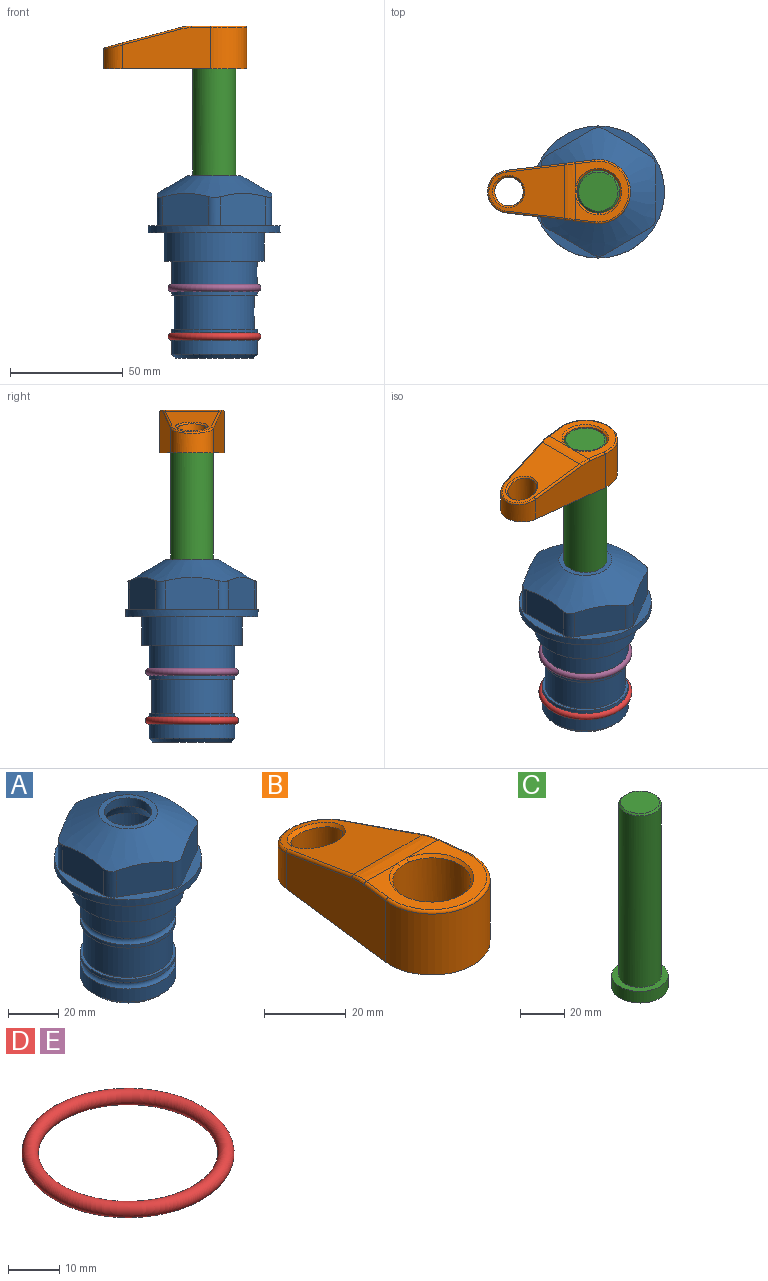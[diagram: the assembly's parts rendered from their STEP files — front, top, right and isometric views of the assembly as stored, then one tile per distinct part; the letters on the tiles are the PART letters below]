
ASSEMBLY  parts=5 mates=4
PART A: 36 faces, bbox 58.7x58.7x81 mm
  f0: cylinder r=17.78mm len=35.56mm, axis (0,0,1), area 1670.8mm2, adj f23,f24,f31
  f1: cylinder r=19.05mm len=38.1mm, axis (0,0,1), area 1191.9mm2, adj f26,f27,f30
  f2: plane 58.66x58.66mm, normal (0,0,-1), area 1150.6mm2, adj f3,f28
  f3: cylinder r=29.33mm len=58.66mm, axis (0,0,-1), area 585.1mm2, adj f2,f4
  f4: plane 58.66x58.66mm, normal (0,0,1), area 475.9mm2, adj f3,f5,f6,f7,f8,f9,f10,f11
  f5: plane 20.32x14.34mm, normal (-0.5,0.87,0), area 324.4mm2, adj f4,f15,f16,f17
  f6: plane 20.32x14.34mm, normal (0.5,0.87,0), area 324.4mm2, adj f4,f14,f15,f17
  f7: plane 23.48x14.34mm, normal (1,0,0), area 324.4mm2, adj f4,f13,f14,f17
  f8: plane 20.32x14.34mm, normal (0.5,-0.87,0), area 324.4mm2, adj f4,f12,f13,f17
  f9: plane 20.32x14.34mm, normal (-0.5,-0.87,0), area 324.4mm2, adj f4,f11,f12,f17
  f10: plane 23.48x14.34mm, normal (-1,0,0), area 324.4mm2, adj f4,f11,f16,f17
  f11: cylinder r=5.08mm len=12.85mm, axis (0,0,-1), area 67.2mm2, adj f4,f9,f10,f17
  f12: cylinder r=5.08mm len=12.85mm, axis (0,0,-1), area 67.2mm2, adj f4,f8,f9,f17
  f13: cylinder r=5.08mm len=12.85mm, axis (0,0,-1), area 67.2mm2, adj f4,f7,f8,f17
  f14: cylinder r=5.08mm len=12.85mm, axis (0,0,-1), area 67.2mm2, adj f4,f6,f7,f17
  f15: cylinder r=5.08mm len=12.85mm, axis (0,0,-1), area 67.2mm2, adj f4,f5,f6,f17
  f16: cylinder r=5.08mm len=12.85mm, axis (0,0,-1), area 67.2mm2, adj f4,f5,f10,f17
  f17: cone r=11.73mm half-angle=60deg, axis (0,0,-1), area 2071.8mm2, adj f5,f6,f7,f8,f9,f10,f11,f12
  f18: plane 23.46x23.46mm, normal (0,0,1), area 147.4mm2, adj f17,f35
  f19: plane 34.93x34.93mm, normal (0,0,-1), area 958mm2, adj f29
  f20: cylinder r=19.05mm len=38.1mm, axis (0,0,1), area 760.1mm2, adj f21,f29
  f21: torus R=19.05mm, axis (0,0,1), area 565.3mm2, adj f20,f22
  f22: cylinder r=19.05mm len=38.1mm, axis (0,0,1), area 190mm2, adj f21,f23
  f23: plane 38.1x38.1mm, normal (0,0,1), area 146.9mm2, adj f0,f22
  f24: plane 38.1x38.1mm, normal (0,0,-1), area 146.9mm2, adj f0,f25
  f25: cylinder r=19.05mm len=38.1mm, axis (0,0,1), area 190mm2, adj f24,f26
  f26: torus R=19.05mm, axis (0,0,1), area 565.3mm2, adj f1,f25
  f27: plane 44.45x44.45mm, normal (0,0,-1), area 411.7mm2, adj f1,f28
  f28: cylinder r=22.23mm len=44.45mm, axis (0,0,1), area 1773.5mm2, adj f2,f27
  f29: cone r=19.05mm half-angle=45deg, axis (0,0,1), area 257.5mm2, adj f19,f20
  f30: cylinder r=3.17mm len=6.75mm, axis (-1,0,0), area 128mm2, adj f1,f33
  f31: cylinder r=3.17mm len=6.35mm, axis (-1,0,0), area 102.5mm2, adj f0,f33
  f32: plane 25.4x25.4mm, normal (0,0,1), area 506.7mm2, adj f33
  f33: cylinder r=12.7mm len=66.42mm, axis (0,0,-1), area 5236.2mm2, adj f30,f31,f32,f34
  f34: cone r=9.53mm half-angle=30deg, axis (0,0,-1), area 443.4mm2, adj f33,f35
  f35: cylinder r=9.53mm len=19.05mm, axis (0,0,-1), area 240.9mm2, adj f18,f34
PART B: 31 faces, bbox 31.7x65.5x19.8 mm
  f0: plane 39.12x18.26mm, normal (0.99,0.12,0), area 612.2mm2, adj f1,f4,f7,f11,f13,f15
  f1: cylinder r=9.53mm len=18.91mm, axis (0,0,-1), area 296.1mm2, adj f0,f2,f7,f17
  f2: plane 39.12x18.26mm, normal (-0.99,0.12,0), area 612.2mm2, adj f1,f4,f7,f12,f14,f16
  f3: cylinder r=6.35mm len=12.7mm, axis (0,0,-1), area 362.4mm2, adj f7,f18
  f4: cylinder r=14.29mm len=28.58mm, axis (0,0,-1), area 882.2mm2, adj f0,f2,f7,f10
  f5: cylinder r=9.53mm len=19.05mm, axis (0,0,-1), area 1092.6mm2, adj f7,f19,f20
  f6: plane 26.99x23.69mm, normal (0,0,1), area 216.2mm2, adj f9,f10,f11,f12,f19
  f7: plane 63.5x28.58mm, normal (0,0,-1), area 661.8mm2, adj f0,f1,f2,f3,f4,f5,f22,f23
  f8: plane 33.52x23.6mm, normal (0,0.26,0.97), area 486mm2, adj f9,f15,f16,f17,f18
  f9: cylinder r=19.05mm len=24.72mm, axis (1,0,0), area 120.4mm2, adj f6,f8,f13,f14,f20
  f10: torus R=13.49mm, axis (0,0,1), area 59mm2, adj f4,f6,f11,f12
  f11: cylinder r=0.79mm len=8.67mm, axis (0.12,-0.99,0), area 10.8mm2, adj f0,f6,f10,f13
  f12: cylinder r=0.79mm len=8.67mm, axis (0.12,0.99,0), area 10.8mm2, adj f2,f6,f10,f14
  f13: bspline ~4.95x1.42mm, area 6.1mm2, adj f0,f9,f11,f15
  f14: bspline ~4.95x1.42mm, area 6.1mm2, adj f2,f9,f12,f16
  f15: cylinder r=0.79mm len=25.95mm, axis (0.12,-0.96,0.26), area 32.9mm2, adj f0,f8,f13,f17
  f16: cylinder r=0.79mm len=25.95mm, axis (0.12,0.96,-0.26), area 32.9mm2, adj f2,f8,f14,f17
  f17: bspline ~18.91x8.38mm, area 30mm2, adj f1,f8,f15,f16
  f18: bspline ~14.29x14.29mm, area 48.3mm2, adj f3,f8
  f19: cone r=9.53mm half-angle=45deg, axis (0,0,1), area 66.5mm2, adj f5,f6,f20
  f20: bspline ~3.22x0.96mm, area 3.5mm2, adj f5,f9,f19
  f21: plane 2.75x2.72mm, normal (0,0,-1), area 2.9mm2, adj f23,f25,f28
  f22: plane 23.05x15.88mm, normal (-0.99,-0.12,0), area 323.6mm2, adj f7,f25,f26,f27,f28,f29
  f23: plane 23.05x15.88mm, normal (0.99,-0.12,0), area 323.6mm2, adj f7,f21,f25,f27,f28,f30
  f24: cylinder r=9.53mm len=10.69mm, axis (0,0,-1), area 114.7mm2, adj f7,f27,f29,f30
  f25: cylinder r=12.7mm len=20.59mm, axis (0,0,-1), area 381.1mm2, adj f7,f21,f22,f23,f26,f28
  f26: plane 2.75x2.72mm, normal (0,0,-1), area 2.9mm2, adj f22,f25,f28
  f27: plane 19.72x18.37mm, normal (0,-0.26,-0.97), area 291.8mm2, adj f22,f23,f24,f28,f29,f30
  f28: cylinder r=15.88mm len=19.92mm, axis (1,0,0), area 54.8mm2, adj f21,f22,f23,f25,f26,f27
  f29: cylinder r=1.59mm len=11mm, axis (0,0,-1), area 34.7mm2, adj f7,f22,f24,f27
  f30: cylinder r=1.59mm len=11mm, axis (0,0,-1), area 34.7mm2, adj f7,f23,f24,f27
PART C: 6 faces, bbox 25.4x25.4x101.6 mm
  f0: plane 17.46x17.46mm, normal (0,0,1), area 239.5mm2, adj f5
  f1: plane 25.4x25.4mm, normal (0,0,-1), area 506.7mm2, adj f2
  f2: cylinder r=12.7mm len=25.4mm, axis (0,0,1), area 506.7mm2, adj f1,f3
  f3: plane 25.4x25.4mm, normal (0,0,1), area 221.7mm2, adj f2,f4
  f4: cylinder r=9.53mm len=94.46mm, axis (0,0,1), area 5653mm2, adj f3,f5
  f5: cone r=8.73mm half-angle=45deg, axis (0,0,-1), area 64.4mm2, adj f0,f4
PART D: 1 faces, bbox 44.7x44.7x3.2 mm
  f0: torus R=19.05mm, axis (0,0,1), area 1193.9mm2
PART E: same geometry as D
PLACE A at identity fixed
PLACE B rot(axis=(0,0,1),90deg) t=(0,0,28.35)mm
PLACE C rot(axis=(0,0,1),90deg) t=(0,0,27.55)mm
PLACE D rot(axis=(1,0,0),180deg) t=(0,0,-70.61)mm
PLACE E at identity
MATE fastened A.f0 <-> D.f0  axis (0,0,1) through (0,0,-46.1)mm
MATE fastened C.f2 <-> B.f4  axis (0,0,1) through (0,0,91.05)mm
MATE cylindrical A.f0 <-> C.f2  axis (0,0,1) through (0,0,-50.55)mm
MATE fastened A.f0 <-> E.f0  axis (0,0,1) through (0,0,-24.51)mm
